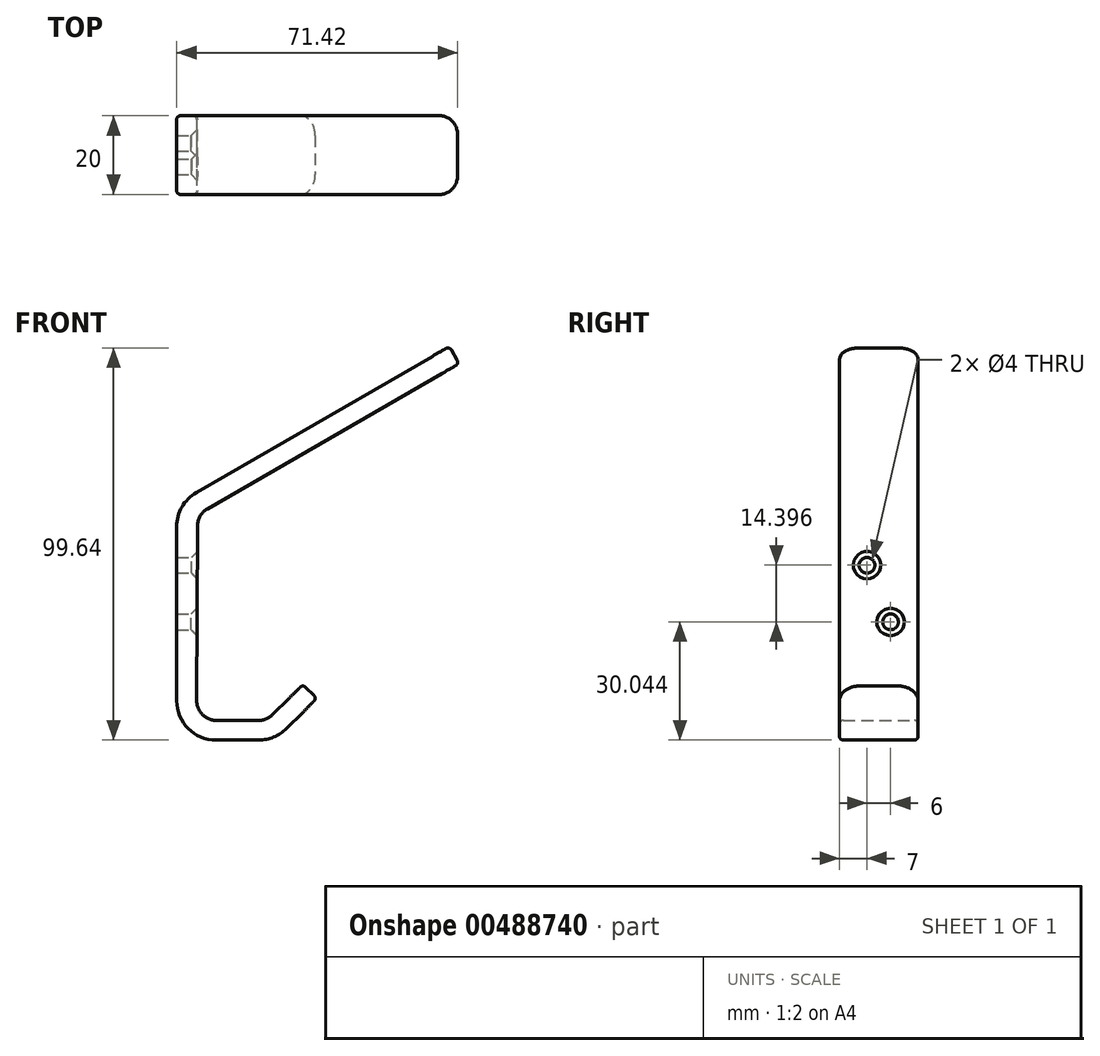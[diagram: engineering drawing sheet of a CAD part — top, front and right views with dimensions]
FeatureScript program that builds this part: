
annotation { "Feature Type Name" : "Feature", "Feature Type Description" : "" }
export const myFeature = defineFeature(function(context is Context, id is Id, definition is map)
    precondition{}
    {
        {
            var Q0;
            Q0=qCreatedBy(makeId("Front.planeOp"),FACE);
            var sketch = newSketch(context, id + "F0", { "sketchPlane" : qUnion([Q0])});
            skLineSegment(sketch, "E0", {"start": v(10.6, 0) * mm, "end": v(0, -10.6) * mm});
            skLineSegment(sketch, "E1", {"start": v(0, -10.6) * mm, "end": v(-25, -10.6) * mm});
            skLineSegment(sketch, "E2", {"start": v(-25, -10.6) * mm, "end": v(-25, 49.4) * mm});
            skLineSegment(sketch, "E3", {"start": v(-25, 49.4) * mm, "end": v(44.28, 89.4) * mm});
            skLineSegment(sketch, "E4", {"start": v(44.28, 89.4) * mm, "end": v(46.78, 85.06) * mm});
            skLineSegment(sketch, "E5", {"start": v(46.78, 85.06) * mm, "end": v(-19.7, 46.68) * mm});
            skLineSegment(sketch, "E6", {"start": v(10.6, 0) * mm, "end": v(7.07, 3.54) * mm});
            skLineSegment(sketch, "E7", {"start": v(7.07, 3.54) * mm, "end": v(-2.07, -5.6) * mm});
            skLineSegment(sketch, "E8", {"start": v(-2.07, -5.6) * mm, "end": v(-19.92, -5.6) * mm});
            skLineSegment(sketch, "E9", {"start": v(-19.92, -5.6) * mm, "end": v(-19.7, 46.68) * mm});
            skSolve(sketch);
        }
        {
            var Q0;
            Q0=makeQuery(id+"F0.imprint","IMPRINT",FACE,{"disambiguationData":[TD([[makeQuery(id+"F0.imprint","IMPRINT",EDGE,{"derivedFrom":sQuery(id+"F0.wireOp",EDGE,"E0")}),-1.0]])]});
            extrude(context, id + "F1", {"entities" : qUnion([Q0]), "depth" : 20 * mm});
        }
        {
            var Q0;
            Q0=makeQuery(id+"F1.opExtrude","SWEPT_EDGE",EDGE,{"disambiguationData":[OSD([sQuery(id+"F0.wireOp",EDGE,"E1"),sQuery(id+"F0.wireOp",EDGE,"E2")])]});
            fillet(context, id + "F2", {"entities" : qUnion([Q0]), "radius" : 10 * mm, "tangentPropagation" : true, "allowEdgeOverflow" : false});
        }
        {
            var Q0;
            Q0=makeQuery(id+"F1.opExtrude","SWEPT_EDGE",EDGE,{"disambiguationData":[OSD([sQuery(id+"F0.wireOp",EDGE,"E2"),sQuery(id+"F0.wireOp",EDGE,"E3")])]});
            fillet(context, id + "F3", {"entities" : qUnion([Q0]), "radius" : 10 * mm, "tangentPropagation" : true, "allowEdgeOverflow" : false});
        }
        {
            var Q0;
            Q0=makeQuery(id+"F1.opExtrude","SWEPT_EDGE",EDGE,{"disambiguationData":[OSD([sQuery(id+"F0.wireOp",EDGE,"E8"),sQuery(id+"F0.wireOp",EDGE,"E9")])]});
            fillet(context, id + "F4", {"entities" : qUnion([Q0]), "radius" : 5 * mm, "tangentPropagation" : true, "allowEdgeOverflow" : false});
        }
        {
            var Q0;
            Q0=makeQuery(id+"F1.opExtrude","SWEPT_EDGE",EDGE,{"disambiguationData":[OSD([sQuery(id+"F0.wireOp",EDGE,"E5"),sQuery(id+"F0.wireOp",EDGE,"E9")])]});
            fillet(context, id + "F5", {"entities" : qUnion([Q0]), "radius" : 5 * mm, "tangentPropagation" : true, "allowEdgeOverflow" : false});
        }
        {
            var Q0;
            Q0=makeQuery(id+"F1.opExtrude","SWEPT_EDGE",EDGE,{"disambiguationData":[OSD([sQuery(id+"F0.wireOp",EDGE,"E0"),sQuery(id+"F0.wireOp",EDGE,"E1")])]});
            fillet(context, id + "F6", {"entities" : qUnion([Q0]), "radius" : 10 * mm, "tangentPropagation" : true, "allowEdgeOverflow" : false});
        }
        {
            var Q0;
            Q0=makeQuery(id+"F1.opExtrude","SWEPT_EDGE",EDGE,{"disambiguationData":[OSD([sQuery(id+"F0.wireOp",EDGE,"E7"),sQuery(id+"F0.wireOp",EDGE,"E8")])]});
            fillet(context, id + "F7", {"entities" : qUnion([Q0]), "radius" : 5 * mm, "tangentPropagation" : true, "allowEdgeOverflow" : false});
        }
        {
            var Q0;
            Q0=makeQuery(id+"F1.opExtrude","CAP_EDGE",EDGE,{"disambiguationData":[OSD([sQuery(id+"F0.wireOp",EDGE,"E6")])],"isStart":false});
            fillet(context, id + "F8", {"entities" : qUnion([Q0]), "radius" : 5 * mm, "tangentPropagation" : true, "allowEdgeOverflow" : false});
        }
        {
            var Q0;
            Q0=makeQuery(id+"F1.opExtrude","CAP_EDGE",EDGE,{"disambiguationData":[OSD([sQuery(id+"F0.wireOp",EDGE,"E6")])],"isStart":true});
            fillet(context, id + "F9", {"entities" : qUnion([Q0]), "radius" : 5 * mm, "tangentPropagation" : true, "allowEdgeOverflow" : false});
        }
        {
            var Q0;
            Q0=makeQuery(id+"F1.opExtrude","CAP_EDGE",EDGE,{"disambiguationData":[OSD([sQuery(id+"F0.wireOp",EDGE,"E4")])],"isStart":false});
            fillet(context, id + "F10", {"entities" : qUnion([Q0]), "radius" : 5 * mm, "tangentPropagation" : true, "allowEdgeOverflow" : false});
        }
        {
            var Q0;
            Q0=makeQuery(id+"F1.opExtrude","CAP_EDGE",EDGE,{"disambiguationData":[OSD([sQuery(id+"F0.wireOp",EDGE,"E4")])],"isStart":true});
            fillet(context, id + "F11", {"entities" : qUnion([Q0]), "radius" : 5 * mm, "tangentPropagation" : true, "allowEdgeOverflow" : false});
        }
        {
            var Q0;
            Q0=makeQuery(id+"F1.opExtrude","CAP_EDGE",EDGE,{"disambiguationData":[OSD([sQuery(id+"F0.wireOp",EDGE,"E7")])],"isStart":true});
            var Q1;
            Q1=makeQuery(id+"F9.opFillet","BLEND_EDGE",EDGE,{"blendedFrom":[makeQuery(id+"F1.opExtrude","CAP_EDGE",EDGE,{"disambiguationData":[OSD([sQuery(id+"F0.wireOp",EDGE,"E6")])],"isStart":true}),makeQuery(id+"F1.opExtrude","SWEPT_FACE",FACE,{"disambiguationData":[OSD([sQuery(id+"F0.wireOp",EDGE,"E0")])]})],"blendedInto":[makeQuery(id+"F1.opExtrude","SWEPT_FACE",FACE,{"disambiguationData":[OSD([sQuery(id+"F0.wireOp",EDGE,"E0")])]})]});
            var Q2;
            Q2=makeQuery(id+"F1.opExtrude","SWEPT_EDGE",EDGE,{"disambiguationData":[OSD([sQuery(id+"F0.wireOp",EDGE,"E0"),sQuery(id+"F0.wireOp",EDGE,"E6")])]});
            var Q3;
            Q3=makeQuery(id+"F8.opFillet","BLEND_EDGE",EDGE,{"blendedFrom":[makeQuery(id+"F1.opExtrude","CAP_EDGE",EDGE,{"disambiguationData":[OSD([sQuery(id+"F0.wireOp",EDGE,"E6")])],"isStart":false}),makeQuery(id+"F1.opExtrude","SWEPT_FACE",FACE,{"disambiguationData":[OSD([sQuery(id+"F0.wireOp",EDGE,"E0")])]})],"blendedInto":[makeQuery(id+"F1.opExtrude","SWEPT_FACE",FACE,{"disambiguationData":[OSD([sQuery(id+"F0.wireOp",EDGE,"E0")])]})]});
            var Q4;
            Q4=makeQuery(id+"F1.opExtrude","CAP_EDGE",EDGE,{"disambiguationData":[OSD([sQuery(id+"F0.wireOp",EDGE,"E0")])],"isStart":false});
            var Q5;
            {var subQ0=sQuery(id+"F0.wireOp",EDGE,"E1");var subQ1=sQuery(id+"F0.wireOp",EDGE,"E0");Q5=makeQuery(id+"F6.opFillet","BLEND_EDGE",EDGE,{"blendedFrom":[makeQuery(id+"F1.opExtrude","SWEPT_EDGE",EDGE,{"disambiguationData":[OSD([subQ1,subQ0])]}),makeQuery(id+"F1.opExtrude","CAP_FACE",FACE,{"disambiguationData":[OSD([subQ1,subQ0,sQuery(id+"F0.wireOp",EDGE,"E2"),sQuery(id+"F0.wireOp",EDGE,"E3"),sQuery(id+"F0.wireOp",EDGE,"E4"),sQuery(id+"F0.wireOp",EDGE,"E5"),sQuery(id+"F0.wireOp",EDGE,"E6"),sQuery(id+"F0.wireOp",EDGE,"E7"),sQuery(id+"F0.wireOp",EDGE,"E8"),sQuery(id+"F0.wireOp",EDGE,"E9")])],"isStart":false})],"blendedInto":[makeQuery(id+"F1.opExtrude","CAP_FACE",FACE,{"disambiguationData":[OSD([subQ1,subQ0,sQuery(id+"F0.wireOp",EDGE,"E2"),sQuery(id+"F0.wireOp",EDGE,"E3"),sQuery(id+"F0.wireOp",EDGE,"E4"),sQuery(id+"F0.wireOp",EDGE,"E5"),sQuery(id+"F0.wireOp",EDGE,"E6"),sQuery(id+"F0.wireOp",EDGE,"E7"),sQuery(id+"F0.wireOp",EDGE,"E8"),sQuery(id+"F0.wireOp",EDGE,"E9")])],"isStart":false})]});}
            var Q6;
            Q6=makeQuery(id+"F1.opExtrude","CAP_EDGE",EDGE,{"disambiguationData":[OSD([sQuery(id+"F0.wireOp",EDGE,"E1")])],"isStart":false});
            var Q7;
            {var subQ0=sQuery(id+"F0.wireOp",EDGE,"E2");var subQ1=sQuery(id+"F0.wireOp",EDGE,"E1");Q7=makeQuery(id+"F2.opFillet","BLEND_EDGE",EDGE,{"blendedFrom":[makeQuery(id+"F1.opExtrude","SWEPT_EDGE",EDGE,{"disambiguationData":[OSD([subQ1,subQ0])]}),makeQuery(id+"F1.opExtrude","CAP_FACE",FACE,{"disambiguationData":[OSD([sQuery(id+"F0.wireOp",EDGE,"E0"),subQ1,subQ0,sQuery(id+"F0.wireOp",EDGE,"E3"),sQuery(id+"F0.wireOp",EDGE,"E4"),sQuery(id+"F0.wireOp",EDGE,"E5"),sQuery(id+"F0.wireOp",EDGE,"E6"),sQuery(id+"F0.wireOp",EDGE,"E7"),sQuery(id+"F0.wireOp",EDGE,"E8"),sQuery(id+"F0.wireOp",EDGE,"E9")])],"isStart":false})],"blendedInto":[makeQuery(id+"F1.opExtrude","CAP_FACE",FACE,{"disambiguationData":[OSD([sQuery(id+"F0.wireOp",EDGE,"E0"),subQ1,subQ0,sQuery(id+"F0.wireOp",EDGE,"E3"),sQuery(id+"F0.wireOp",EDGE,"E4"),sQuery(id+"F0.wireOp",EDGE,"E5"),sQuery(id+"F0.wireOp",EDGE,"E6"),sQuery(id+"F0.wireOp",EDGE,"E7"),sQuery(id+"F0.wireOp",EDGE,"E8"),sQuery(id+"F0.wireOp",EDGE,"E9")])],"isStart":false})]});}
            var Q8;
            Q8=makeQuery(id+"F1.opExtrude","CAP_EDGE",EDGE,{"disambiguationData":[OSD([sQuery(id+"F0.wireOp",EDGE,"E2")])],"isStart":false});
            var Q9;
            {var subQ0=sQuery(id+"F0.wireOp",EDGE,"E3");var subQ1=sQuery(id+"F0.wireOp",EDGE,"E2");Q9=makeQuery(id+"F3.opFillet","BLEND_EDGE",EDGE,{"blendedFrom":[makeQuery(id+"F1.opExtrude","SWEPT_EDGE",EDGE,{"disambiguationData":[OSD([subQ1,subQ0])]}),makeQuery(id+"F1.opExtrude","CAP_FACE",FACE,{"disambiguationData":[OSD([sQuery(id+"F0.wireOp",EDGE,"E0"),sQuery(id+"F0.wireOp",EDGE,"E1"),subQ1,subQ0,sQuery(id+"F0.wireOp",EDGE,"E4"),sQuery(id+"F0.wireOp",EDGE,"E5"),sQuery(id+"F0.wireOp",EDGE,"E6"),sQuery(id+"F0.wireOp",EDGE,"E7"),sQuery(id+"F0.wireOp",EDGE,"E8"),sQuery(id+"F0.wireOp",EDGE,"E9")])],"isStart":false})],"blendedInto":[makeQuery(id+"F1.opExtrude","CAP_FACE",FACE,{"disambiguationData":[OSD([sQuery(id+"F0.wireOp",EDGE,"E0"),sQuery(id+"F0.wireOp",EDGE,"E1"),subQ1,subQ0,sQuery(id+"F0.wireOp",EDGE,"E4"),sQuery(id+"F0.wireOp",EDGE,"E5"),sQuery(id+"F0.wireOp",EDGE,"E6"),sQuery(id+"F0.wireOp",EDGE,"E7"),sQuery(id+"F0.wireOp",EDGE,"E8"),sQuery(id+"F0.wireOp",EDGE,"E9")])],"isStart":false})]});}
            var Q10;
            Q10=makeQuery(id+"F1.opExtrude","CAP_EDGE",EDGE,{"disambiguationData":[OSD([sQuery(id+"F0.wireOp",EDGE,"E3")])],"isStart":false});
            var Q11;
            {var subQ0=sQuery(id+"F0.wireOp",EDGE,"E9");var subQ1=sQuery(id+"F0.wireOp",EDGE,"E8");Q11=makeQuery(id+"F4.opFillet","BLEND_EDGE",EDGE,{"blendedFrom":[makeQuery(id+"F1.opExtrude","SWEPT_EDGE",EDGE,{"disambiguationData":[OSD([subQ1,subQ0])]}),makeQuery(id+"F1.opExtrude","CAP_FACE",FACE,{"disambiguationData":[OSD([sQuery(id+"F0.wireOp",EDGE,"E0"),sQuery(id+"F0.wireOp",EDGE,"E1"),sQuery(id+"F0.wireOp",EDGE,"E2"),sQuery(id+"F0.wireOp",EDGE,"E3"),sQuery(id+"F0.wireOp",EDGE,"E4"),sQuery(id+"F0.wireOp",EDGE,"E5"),sQuery(id+"F0.wireOp",EDGE,"E6"),sQuery(id+"F0.wireOp",EDGE,"E7"),subQ1,subQ0])],"isStart":false})],"blendedInto":[makeQuery(id+"F1.opExtrude","CAP_FACE",FACE,{"disambiguationData":[OSD([sQuery(id+"F0.wireOp",EDGE,"E0"),sQuery(id+"F0.wireOp",EDGE,"E1"),sQuery(id+"F0.wireOp",EDGE,"E2"),sQuery(id+"F0.wireOp",EDGE,"E3"),sQuery(id+"F0.wireOp",EDGE,"E4"),sQuery(id+"F0.wireOp",EDGE,"E5"),sQuery(id+"F0.wireOp",EDGE,"E6"),sQuery(id+"F0.wireOp",EDGE,"E7"),subQ1,subQ0])],"isStart":false})]});}
            var Q12;
            Q12=makeQuery(id+"F1.opExtrude","CAP_EDGE",EDGE,{"disambiguationData":[OSD([sQuery(id+"F0.wireOp",EDGE,"E8")])],"isStart":false});
            var Q13;
            {var subQ0=sQuery(id+"F0.wireOp",EDGE,"E8");var subQ1=sQuery(id+"F0.wireOp",EDGE,"E7");Q13=makeQuery(id+"F7.opFillet","BLEND_EDGE",EDGE,{"blendedFrom":[makeQuery(id+"F1.opExtrude","SWEPT_EDGE",EDGE,{"disambiguationData":[OSD([subQ1,subQ0])]}),makeQuery(id+"F1.opExtrude","CAP_FACE",FACE,{"disambiguationData":[OSD([sQuery(id+"F0.wireOp",EDGE,"E0"),sQuery(id+"F0.wireOp",EDGE,"E1"),sQuery(id+"F0.wireOp",EDGE,"E2"),sQuery(id+"F0.wireOp",EDGE,"E3"),sQuery(id+"F0.wireOp",EDGE,"E4"),sQuery(id+"F0.wireOp",EDGE,"E5"),sQuery(id+"F0.wireOp",EDGE,"E6"),subQ1,subQ0,sQuery(id+"F0.wireOp",EDGE,"E9")])],"isStart":false})],"blendedInto":[makeQuery(id+"F1.opExtrude","CAP_FACE",FACE,{"disambiguationData":[OSD([sQuery(id+"F0.wireOp",EDGE,"E0"),sQuery(id+"F0.wireOp",EDGE,"E1"),sQuery(id+"F0.wireOp",EDGE,"E2"),sQuery(id+"F0.wireOp",EDGE,"E3"),sQuery(id+"F0.wireOp",EDGE,"E4"),sQuery(id+"F0.wireOp",EDGE,"E5"),sQuery(id+"F0.wireOp",EDGE,"E6"),subQ1,subQ0,sQuery(id+"F0.wireOp",EDGE,"E9")])],"isStart":false})]});}
            var Q14;
            Q14=makeQuery(id+"F1.opExtrude","CAP_EDGE",EDGE,{"disambiguationData":[OSD([sQuery(id+"F0.wireOp",EDGE,"E7")])],"isStart":false});
            var Q15;
            Q15=makeQuery(id+"F8.opFillet","BLEND_EDGE",EDGE,{"blendedFrom":[makeQuery(id+"F1.opExtrude","CAP_EDGE",EDGE,{"disambiguationData":[OSD([sQuery(id+"F0.wireOp",EDGE,"E6")])],"isStart":false}),makeQuery(id+"F1.opExtrude","SWEPT_FACE",FACE,{"disambiguationData":[OSD([sQuery(id+"F0.wireOp",EDGE,"E7")])]})],"blendedInto":[makeQuery(id+"F1.opExtrude","SWEPT_FACE",FACE,{"disambiguationData":[OSD([sQuery(id+"F0.wireOp",EDGE,"E7")])]})]});
            var Q16;
            Q16=makeQuery(id+"F1.opExtrude","CAP_EDGE",EDGE,{"disambiguationData":[OSD([sQuery(id+"F0.wireOp",EDGE,"E9")])],"isStart":false});
            var Q17;
            {var subQ0=sQuery(id+"F0.wireOp",EDGE,"E9");var subQ1=sQuery(id+"F0.wireOp",EDGE,"E5");Q17=makeQuery(id+"F5.opFillet","BLEND_EDGE",EDGE,{"blendedFrom":[makeQuery(id+"F1.opExtrude","SWEPT_EDGE",EDGE,{"disambiguationData":[OSD([subQ1,subQ0])]}),makeQuery(id+"F1.opExtrude","CAP_FACE",FACE,{"disambiguationData":[OSD([sQuery(id+"F0.wireOp",EDGE,"E0"),sQuery(id+"F0.wireOp",EDGE,"E1"),sQuery(id+"F0.wireOp",EDGE,"E2"),sQuery(id+"F0.wireOp",EDGE,"E3"),sQuery(id+"F0.wireOp",EDGE,"E4"),subQ1,sQuery(id+"F0.wireOp",EDGE,"E6"),sQuery(id+"F0.wireOp",EDGE,"E7"),sQuery(id+"F0.wireOp",EDGE,"E8"),subQ0])],"isStart":false})],"blendedInto":[makeQuery(id+"F1.opExtrude","CAP_FACE",FACE,{"disambiguationData":[OSD([sQuery(id+"F0.wireOp",EDGE,"E0"),sQuery(id+"F0.wireOp",EDGE,"E1"),sQuery(id+"F0.wireOp",EDGE,"E2"),sQuery(id+"F0.wireOp",EDGE,"E3"),sQuery(id+"F0.wireOp",EDGE,"E4"),subQ1,sQuery(id+"F0.wireOp",EDGE,"E6"),sQuery(id+"F0.wireOp",EDGE,"E7"),sQuery(id+"F0.wireOp",EDGE,"E8"),subQ0])],"isStart":false})]});}
            var Q18;
            Q18=makeQuery(id+"F1.opExtrude","CAP_EDGE",EDGE,{"disambiguationData":[OSD([sQuery(id+"F0.wireOp",EDGE,"E5")])],"isStart":false});
            var Q19;
            Q19=makeQuery(id+"F10.opFillet","BLEND_EDGE",EDGE,{"blendedFrom":[makeQuery(id+"F1.opExtrude","CAP_EDGE",EDGE,{"disambiguationData":[OSD([sQuery(id+"F0.wireOp",EDGE,"E4")])],"isStart":false}),makeQuery(id+"F1.opExtrude","SWEPT_FACE",FACE,{"disambiguationData":[OSD([sQuery(id+"F0.wireOp",EDGE,"E5")])]})],"blendedInto":[makeQuery(id+"F1.opExtrude","SWEPT_FACE",FACE,{"disambiguationData":[OSD([sQuery(id+"F0.wireOp",EDGE,"E5")])]})]});
            var Q20;
            Q20=makeQuery(id+"F1.opExtrude","SWEPT_EDGE",EDGE,{"disambiguationData":[OSD([sQuery(id+"F0.wireOp",EDGE,"E4"),sQuery(id+"F0.wireOp",EDGE,"E5")])]});
            var Q21;
            Q21=makeQuery(id+"F1.opExtrude","SWEPT_EDGE",EDGE,{"disambiguationData":[OSD([sQuery(id+"F0.wireOp",EDGE,"E3"),sQuery(id+"F0.wireOp",EDGE,"E4")])]});
            var Q22;
            Q22=makeQuery(id+"F10.opFillet","BLEND_EDGE",EDGE,{"blendedFrom":[makeQuery(id+"F1.opExtrude","CAP_EDGE",EDGE,{"disambiguationData":[OSD([sQuery(id+"F0.wireOp",EDGE,"E4")])],"isStart":false}),makeQuery(id+"F1.opExtrude","SWEPT_FACE",FACE,{"disambiguationData":[OSD([sQuery(id+"F0.wireOp",EDGE,"E3")])]})],"blendedInto":[makeQuery(id+"F1.opExtrude","SWEPT_FACE",FACE,{"disambiguationData":[OSD([sQuery(id+"F0.wireOp",EDGE,"E3")])]})]});
            var Q23;
            Q23=makeQuery(id+"F1.opExtrude","SWEPT_EDGE",EDGE,{"disambiguationData":[OSD([sQuery(id+"F0.wireOp",EDGE,"E6"),sQuery(id+"F0.wireOp",EDGE,"E7")])]});
            var Q24;
            Q24=makeQuery(id+"F9.opFillet","BLEND_EDGE",EDGE,{"blendedFrom":[makeQuery(id+"F1.opExtrude","CAP_EDGE",EDGE,{"disambiguationData":[OSD([sQuery(id+"F0.wireOp",EDGE,"E6")])],"isStart":true}),makeQuery(id+"F1.opExtrude","SWEPT_FACE",FACE,{"disambiguationData":[OSD([sQuery(id+"F0.wireOp",EDGE,"E7")])]})],"blendedInto":[makeQuery(id+"F1.opExtrude","SWEPT_FACE",FACE,{"disambiguationData":[OSD([sQuery(id+"F0.wireOp",EDGE,"E7")])]})]});
            fillet(context, id + "F12", {"entities" : qUnion([Q0, Q1, Q2, Q3, Q4, Q5, Q6, Q7, Q8, Q9, Q10, Q11, Q12, Q13, Q14, Q15, Q16, Q17, Q18, Q19, Q20, Q21, Q22, Q23, Q24]), "radius" : 1 * mm, "tangentPropagation" : true, "allowEdgeOverflow" : false});
        }
        {
            var Q0;
            Q0=makeQuery(id+"F1.opExtrude","SWEPT_FACE",FACE,{"disambiguationData":[OSD([sQuery(id+"F0.wireOp",EDGE,"E9")])]});
            var sketch = newSketch(context, id + "F13", { "sketchPlane" : qUnion([Q0])});
            skPoint(sketch, "E10", {"position": v(-13, 33.72) * mm});
            skPoint(sketch, "E11", {"position": v(-7, 19.33) * mm});
            skSolve(sketch);
        }
        {
            var Q0;
            Q0=sQuery(id+"F13.wireOp",VERTEX,"E10");
            var Q1;
            Q1=sQuery(id+"F13.wireOp",VERTEX,"E11");
            var Q2;
            Q2=makeQuery(id+"F1.opExtrude","SWEPT_BODY",BODY,{"disambiguationData":[OSD([sQuery(id+"F0.wireOp",EDGE,"E0"),sQuery(id+"F0.wireOp",EDGE,"E1"),sQuery(id+"F0.wireOp",EDGE,"E2"),sQuery(id+"F0.wireOp",EDGE,"E3"),sQuery(id+"F0.wireOp",EDGE,"E4"),sQuery(id+"F0.wireOp",EDGE,"E5"),sQuery(id+"F0.wireOp",EDGE,"E6"),sQuery(id+"F0.wireOp",EDGE,"E7"),sQuery(id+"F0.wireOp",EDGE,"E8"),sQuery(id+"F0.wireOp",EDGE,"E9")])]});
            hole(context, id + "F14", {"style" : HoleStyle.C_SINK, "endStyle" : HoleEndStyle.THROUGH, "holeDiameter" : 4 * mm, "cSinkDiameter" : 7 * mm, "cSinkAngle" : 90 * degree, "isTappedThrough" : true, "tappedDepth" : 12 * mm, "tapClearance" : 3, "locations" : qUnion([Q0, Q1]), "scope" : qUnion([Q2])});
        }
    });
